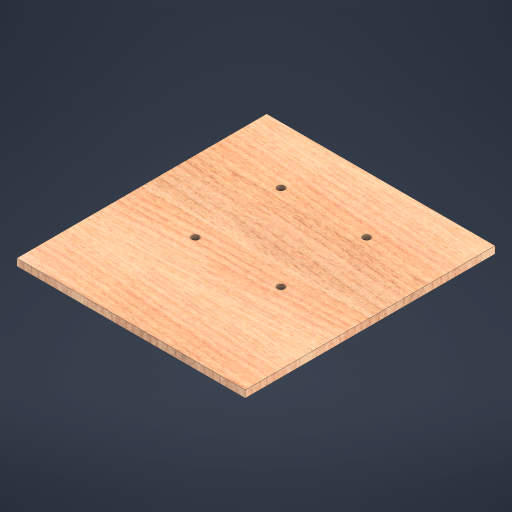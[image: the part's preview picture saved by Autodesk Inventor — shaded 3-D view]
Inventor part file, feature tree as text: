
AUTODESK INVENTOR PART (.ipt)
format: ipt  version: 2023 (Build 270158000, 158)  size: 344,576 bytes
history: native  units: mm
features: sketch x3, hole x2, other x1, extrude x1
ambient origin geometry x8: Origin, YZ Plane, XZ Plane, XY Plane, X Axis, Y Axis, Z Axis, Center Point
bodies: Body1 (feature_tree)
feature tree (7):
  other  "Těleso1"
  extrude  "Vysunutí1"  Depth=320.0mm
  hole  "Díra1"  [1 undecoded]
  hole  "Díra2"  [1 undecoded]
  sketch  "Náčrt1"
  sketch  "Náčrt3"
  sketch  "Náčrt4"
note: 2 required parameter values undecoded (feature->parameter linkage not recoverable at this tier; creation-order binding heuristic only, values carry confidence <= 0.55)
